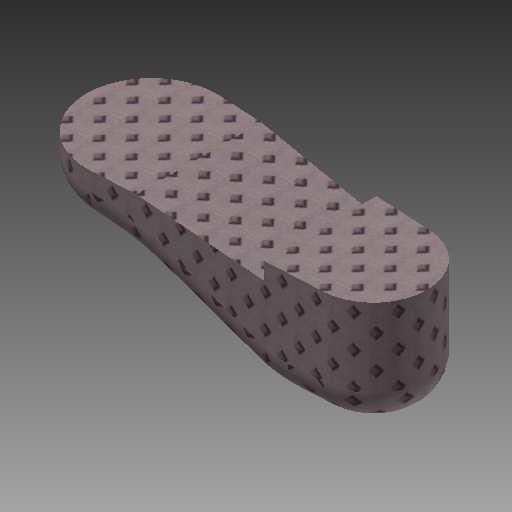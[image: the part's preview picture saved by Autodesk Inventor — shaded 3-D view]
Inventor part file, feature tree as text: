
AUTODESK INVENTOR PART (.ipt)
format: ipt  version: 2022 (Build 260153000, 153)  size: 359,936 bytes
history: native  units: mm (DEFAULTED — no unit token found)
features: extrude x2, fillet x2, sketch x2, other x1
ambient origin geometry x8: Origin, YZ Plane, XZ Plane, XY Plane, X Axis, Y Axis, Z Axis, Center Point
bodies: Solid1 (feature_tree)
feature tree (7):
  other  "iMandy - 2D BODY"
  extrude  "Extrusion1"  Depth=10.0mm
  extrude  "Extrusion2"  Depth=24.9174mm
  fillet  "Fillet2"  Radius=124.587mm
  fillet  "Fillet3"  [1 undecoded]
  sketch  "Sketch3"  dims[d1=10.0mm d34=249.174mm]
  sketch  "Sketch4"  dims[d35=77.978mm d36=94.9452mm d38=124.587mm d39=0.0mm d40=77.978mm d43=24.9174mm d44=0.0mm d45=124.587mm d46=24.9174mm d52=82.22742mm d53=32.39262mm d54=4.014257mm d56=1.22173mm d57=82.22742mm d59=74.7522mm d60=12.7mm]
note: 1 required parameter value undecoded (feature->parameter linkage not recoverable at this tier; creation-order binding heuristic only, values carry confidence <= 0.55)
